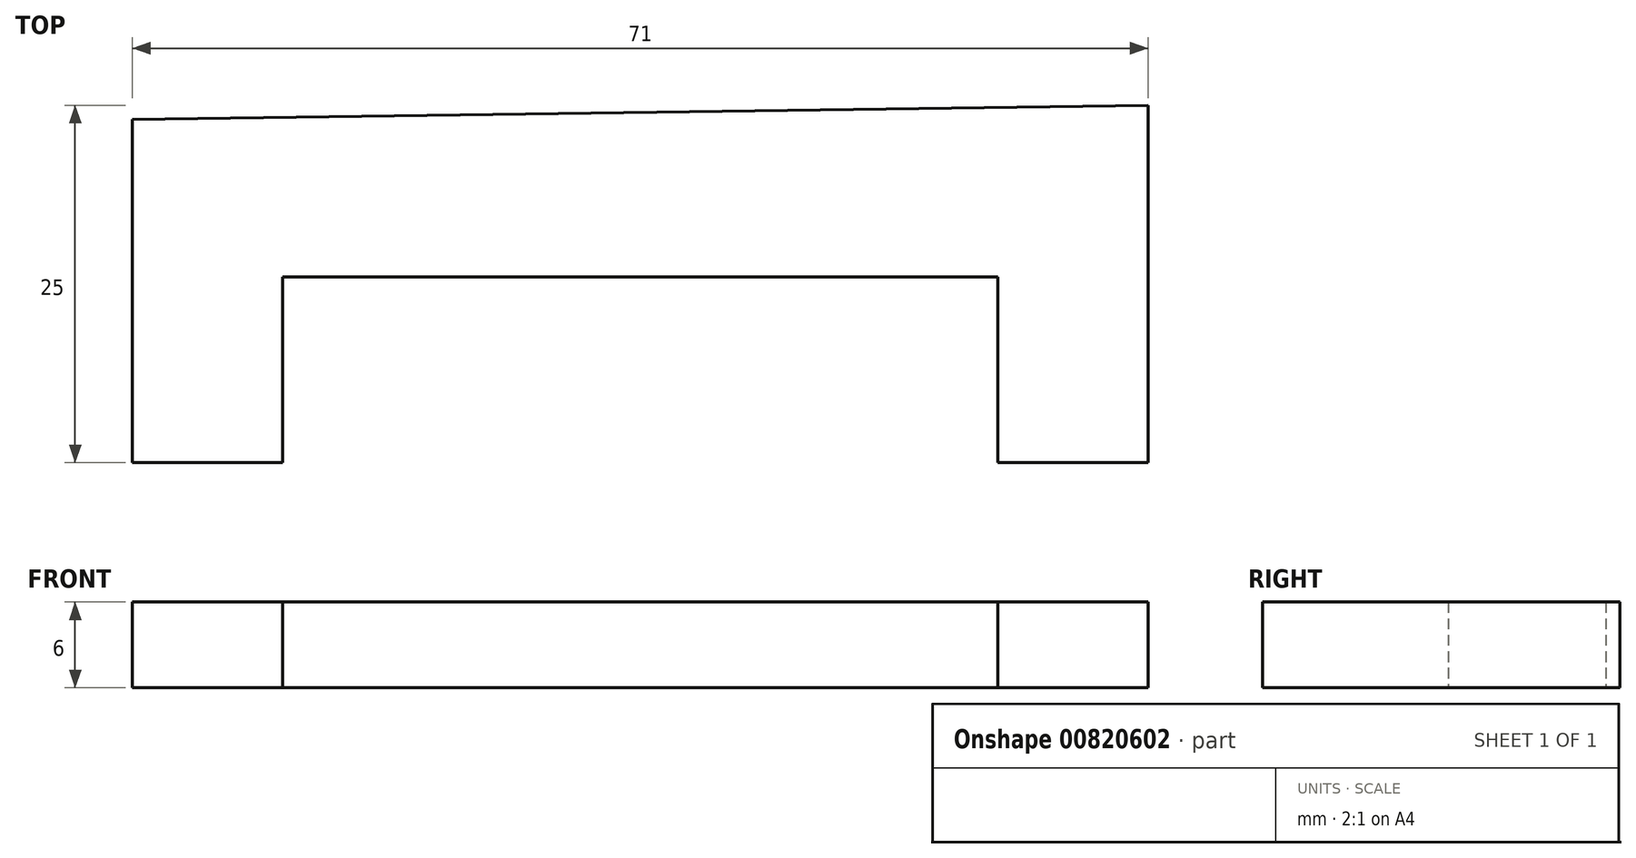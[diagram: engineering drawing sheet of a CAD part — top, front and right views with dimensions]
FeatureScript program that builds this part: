
annotation { "Feature Type Name" : "Feature", "Feature Type Description" : "" }
export const myFeature = defineFeature(function(context is Context, id is Id, definition is map)
    precondition{}
    {
        {
            var Q0;
            Q0=qCreatedBy(makeId("Top.planeOp"),FACE);
            var sketch = newSketch(context, id + "F0", { "sketchPlane" : qUnion([Q0])});
            skLineSegment(sketch, "E0", {"start": v(-57.16, -35.47) * mm, "end": v(-67.66, -35.47) * mm});
            skLineSegment(sketch, "E1", {"start": v(-67.66, -35.47) * mm, "end": v(-67.66, -22.47) * mm});
            skLineSegment(sketch, "E2", {"start": v(-67.66, -22.47) * mm, "end": v(-117.66, -22.47) * mm});
            skLineSegment(sketch, "E3", {"start": v(-117.66, -22.47) * mm, "end": v(-117.66, -35.47) * mm});
            skLineSegment(sketch, "E4", {"start": v(-117.66, -35.47) * mm, "end": v(-128.16, -35.47) * mm});
            skLineSegment(sketch, "E5", {"start": v(-128.16, -35.47) * mm, "end": v(-128.16, -11.47) * mm});
            skLineSegment(sketch, "E6", {"start": v(-128.16, -11.47) * mm, "end": v(-57.16, -10.47) * mm});
            skLineSegment(sketch, "E7", {"start": v(-57.16, -10.47) * mm, "end": v(-57.16, -35.47) * mm});
            skSolve(sketch);
        }
        {
            var Q0;
            Q0 = qSketchRegion(id + "F0", true);
            extrude(context, id + "F1", {"entities" : qUnion([Q0]), "depth" : 6 * mm, "offsetDistance" : 25 * mm});
        }
    });
